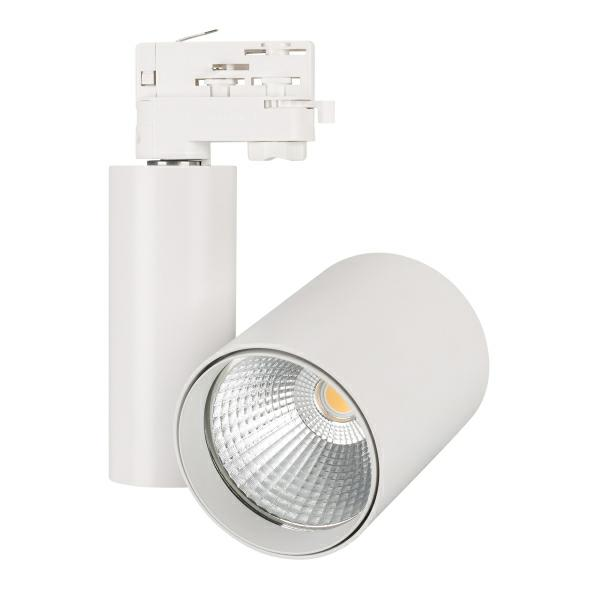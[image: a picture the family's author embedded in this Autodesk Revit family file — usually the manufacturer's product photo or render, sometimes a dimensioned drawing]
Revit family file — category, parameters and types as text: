
# Revit family: SHOP-4TR-R100
name_source: partatom
category: Осветительные приборы
revit_build: Autodesk Revit 2017 (Build: 20160225_1515(x64)
units: mm (PartAtom-declared; Revit-internal decimal feet)

## family parameters
Всегда вертикально = Да
Источник света = Нет
На основе рабочей плоскости = Нет
Общий = Нет
При загрузке вырезать с полостями = Нет
Размер круглого соединителя = Использовать диаметр
Тип детали = Нормальный
Точка расчета площади = Нет

## types (20) — shared parameters
ADSK_Единица измерения = шт.
ADSK_Завод-изготовитель = ARLIGHT
ADSK_Классификация нагрузок = Освещение
ADSK_Количество фаз = 1
ADSK_Количество фаз числовое = 1
ADSK_Коэффициент мощности = 0.95
ADSK_Наименование = Светильник
ADSK_Напряжение = 230 В
ADSK_Номинальная мощность = 40 Вт
ADSK_Полная мощность = 42 В·А
ADSK_Размер_Высота = 190 мм
ADSK_Размер_Диаметр = 100 мм
ADSK_Размер_Длина = 130 мм
ADSK_Размер_Радиус = 50 мм
ADSK_Размер_Ширина = 160 мм
ADSK_Ток = 0 А
ARL_Драйвер = Встроенный (30-42V, 1000mA)
ARL_Класс защиты от поражения электрическим током = I
ARL_Класс пылевлагозащиты = IP20
ARL_Область использования = Для локального освещения в торговых, демонстрационных, офисных, жилых и других помещениях
ARL_Рабочая температура окружающей среды = -25...+45 °C
ARL_Способ монтажа = на трек 3-фазный
ARL_Тип товара = Светильник
ARL_Угол обзора = 24°
URL = https://arlight.ru
Группа модели = Светильники
Изготовитель = ARLIGHT
Изготовитель (сайт) = www.arlight.ru
Изготовитель (телефон) = 8 800 505 26 29
Исходная интенсивность (лм) = 4000
Полная установленная мощность = 42 В·А
Разработчик = НТЦ Конструктор
Разработчик (URL) = https://constructor.ru
Разработчик (телефон) = +7 (495) 781-05-35

## per-type parameters (varying)
| type | ADSK_Код изделия | ADSK_Марка | ADSK_Масса_Текст | ARL_Индекс цветопередачи | ARL_Материал корпуса | ARL_Обозначение корпуса | ARL_Серия | ARL_Цвет покрытия | ARL_Цвет свечения | Комментарии к типоразмеру | Описание | Фотометрия | Цветовая температура (К) |
| 026278 Светильник LGD-SHOP-4TR-R100-40W White6000 (WH, 24 deg) | Арт. 026278 | LGD-SHOP-4TR-R100-40W White6000 | 1.32
1.332
1.332 | >90 | Металл, белый | Корпус круглый, металл, цвет белый | SHOP | Белый | Белый 6000K | Арт. 026278 | Светильник подвесной для треков/шин 4 провода, 40 Вт. Цвет свечения БЕЛЫЙ 6000K, световой поток 3600-4000лм, угол 24°, CRI>90. Корпус круглый, металл, цвет белый, IP20. Размеры ØDxHxL: Ø100х190х130 мм. Входное напряжение AC220-240V, мощность 40 Вт. Драйвер встроенный (30-42V, 1000mA) | SHOP-4TR-R100 IES Data : 026278_LGD-SHOP-4TR-R100-40W White6000 (WH, 24 deg) | 6000 |
| 025398 Светильник LGD-SHOP-4TR-R100-40W Day4000 (WH, 24 deg) | Арт. 025398 | LGD-SHOP-4TR-R100-40W Day4000 | 1.32
1.25
1.332 | >90 | Металл, белый | Корпус круглый, металл, цвет белый | SHOP | Белый | Дневной 4000K | Арт. 025398 | Светильник подвесной для треков/шин 4 провода, 40 Вт. Цвет свечения ДНЕВНОЙ 4000K, световой поток 3600-4000лм, угол 24°, CRI>90. Корпус круглый, металл, цвет белый, IP20. Размеры ØDxHxL: Ø100х190х130 мм. Входное напряжение AC220-240V, мощность 40 Вт. Драйвер встроенный (30-42V, 1000mA) | SHOP-4TR-R100 IES Data : 025398_LGD-SHOP-4TR-R100-40W Day4000 (WH, 24 deg) | 4000 |
| 026279 Светильник LGD-SHOP-4TR-R100-40W Warm3000 (WH, 24 deg) | Арт. 026279 | LGD-SHOP-4TR-R100-40W Warm3000 | 1.32
1.332
1.332 | >90 | Металл, белый | Корпус круглый, металл, цвет белый | SHOP | Белый | Теплый 3000K | Арт. 026279 | Светильник подвесной для треков/шин 4 провода, 40 Вт. Цвет свечения ТЕПЛЫЙ 3000K, световой поток 3600-4000лм, угол 24°, CRI>90. Корпус круглый, металл, цвет белый, IP20. Размеры ØDxHxL: Ø100х190х130 мм. Входное напряжение AC220-240V, мощность 40 Вт. Драйвер встроенный (30-42V, 1000mA) | SHOP-4TR-R100 IES Data : 026279_LGD-SHOP-4TR-R100-40W Warm3000 (WH, 24 deg) | 3000 |
| 026425 Светильник LGD-SHOP-PREMIUM-4TR-R100-40W Day4000 (WH, 24 deg) | Арт. 026425 | LGD-SHOP-PREMIUM-4TR-R100-40W Day4000 | 1.32
1.33
1.332 | >90 | Металл, белый | Корпус круглый, металл, цвет белый | SHOP | Белый | Дневной 4000K | Арт. 026425 | Светильник подвесной для треков/шин 4 провода, 40 Вт. Цвет свечения ДНЕВНОЙ 4000K, световой поток 3600-4000лм, угол 24°, CRI>90. Корпус круглый, металл, цвет белый, IP20. Размеры ØDxHxL: Ø100х190х130 мм. Входное напряжение AC220-240V, мощность 30 Вт. Драйвер встроенный (30-42V, 1000mA) | SHOP-4TR-R100 IES Data : 026425_LGD-SHOP-PREMIUM-4TR-R100-40W Day4000 (WH, 24 deg) | 4000 |
| 026426 Светильник LGD-SHOP-PREMIUM-4TR-R100-40W Warm3000 (WH, 24 deg) | Арт. 026426 | LGD-SHOP-PREMIUM-4TR-R100-40W Warm3000 | 1.32
1.332
1.332 | >90 | Металл, белый | Корпус круглый, металл, цвет белый | SHOP | Белый | Теплый 3000K | Арт. 026426 | Светильник подвесной для треков/шин 4 провода, 40 Вт. Цвет свечения ТЕПЛЫЙ 3000K, световой поток 3600-4000лм, угол 24°, CRI>90. Корпус круглый, металл, цвет белый, IP20. Размеры ØDxHxL: Ø100х190х130 мм. Входное напряжение AC220-240V, мощность 40 Вт. Драйвер встроенный (30-42V, 1000mA) | SHOP-4TR-R100 IES Data : 026426_LGD-SHOP-PREMIUM-4TR-R100-40W Warm3000 (WH, 24 deg) | 3000 |
| 026281 Светильник LGD-SHOP-4TR-R100-40W White6000 (BK, 24 deg) | Арт. 026281 | LGD-SHOP-4TR-R100-40W White6000 | 1.32
1.332
1.332 | >90 | Металл, чёрный | Корпус круглый, металл, цвет черный | SHOP | Черный | Белый 6000K | Арт. 026281 | Светильник подвесной для треков/шин 4 провода, 40 Вт. Цвет свечения БЕЛЫЙ 6000K, световой поток 3600-4000лм, угол 24°, CRI>90. Корпус круглый, металл, цвет черный, IP20. Размеры ØDxHxL: Ø100х190х130 мм. Входное напряжение AC220-240V, мощность 40 Вт. Драйвер встроенный (30-42V, 1000mA) | SHOP-4TR-R100 IES Data : 026281_LGD-SHOP-4TR-R100-40W White6000 (BK, 24 deg) | 6000 |
| 026282 Светильник LGD-SHOP-4TR-R100-40W Day4000 (BK, 24 deg) | Арт. 026282 | LGD-SHOP-4TR-R100-40W Day4000 | 1.32
1.332
1.332 | >90 | Металл, чёрный | Корпус круглый, металл, цвет черный | SHOP | Черный | Дневной 4000K | Арт. 026282 | Светильник подвесной для треков/шин 4 провода, 40 Вт. Цвет свечения ДНЕВНОЙ 4000K, световой поток 3600-4000лм, угол 24°, CRI>90. Корпус круглый, металл, цвет черный, IP20. Размеры ØDxHxL: Ø100х190х130 мм. Входное напряжение AC220-240V, мощность 40 Вт. Драйвер встроенный (30-42V, 1000mA) | SHOP-4TR-R100 IES Data : 026282_LGD-SHOP-4TR-R100-40W Day4000 (BK, 24 deg) | 4000 |
| 026284 Светильник LGD-SHOP-4TR-R100-40W Warm3000 (BK, 24 deg) | Арт. 026284 | LGD-SHOP-4TR-R100-40W Warm3000 | 1.32
1.332
1.332 | >90 | Металл, чёрный | Корпус круглый, металл, цвет черный | SHOP | Черный | Теплый 3000K | Арт. 026284 | Светильник подвесной для треков/шин 4 провода, 40 Вт. Цвет свечения ТЕПЛЫЙ 3000K, световой поток 3600-4000лм, угол 24°, CRI>90. Корпус круглый, металл, цвет черный, IP20. Размеры ØDxHxL: Ø100х190х130 мм. Входное напряжение AC220-240V, мощность 40 Вт. Драйвер встроенный (30-42V, 1000mA) | SHOP-4TR-R100 IES Data : 026284_LGD-SHOP-4TR-R100-40W Warm3000 (BK, 24 deg) | 3000 |
| 026428 Светильник LGD-SHOP-PREMIUM-4TR-R100-40W Day4000 (BK, 24 deg) | Арт. 026428 | LGD-SHOP-PREMIUM-4TR-R100-40W Day4000 | 1.32
1.332
1.332 | >90 | Металл, чёрный | Корпус круглый, металл, цвет черный | SHOP | Черный | Дневной 4000K | Арт. 026428 | Светильник подвесной для треков/шин 4 провода, 40 Вт. Цвет свечения ДНЕВНОЙ 4000K, световой поток 3600-4000лм, угол 24°, CRI>90. Корпус круглый, металл, цвет черный, IP20. Размеры ØDxHxL: Ø100х190х130 мм. Входное напряжение AC220-240V, мощность 40 Вт. Драйвер встроенный (30-42V, 1000mA) | SHOP-4TR-R100 IES Data : 026428_LGD-SHOP-PREMIUM-4TR-R100-40W Day4000 (BK, 24 deg) | 4000 |
| 026429 Светильник LGD-SHOP-PREMIUM-4TR-R100-40W Warm3000 (BK, 24 deg) | Арт. 026429 | LGD-SHOP-PREMIUM-4TR-R100-40W Warm3000 | 1.32
1.332
1.332 | >90 | Металл, чёрный | Корпус круглый, металл, цвет черный | SHOP | Черный | Теплый 3000K | Арт. 026429 | Светильник подвесной для треков/шин 4 провода, 40 Вт. Цвет свечения ТЕПЛЫЙ 3000K, световой поток 3600-4000лм, угол 24°, CRI>90. Корпус круглый, металл, цвет черный, IP20. Размеры ØDxHxL: Ø100х190х130 мм. Входное напряжение AC220-240V, мощность 40 Вт. Драйвер встроенный (30-42V, 1000mA) | SHOP-4TR-R100 IES Data : 026429_LGD-SHOP-PREMIUM-4TR-R100-40W Warm3000 (BK, 24 deg) | 3000 |
| 026387 Светильник LGD-SHOP-4TR-R100-40W Cool SP7500-Fish (WH, 24 deg) | Арт. 026387 | LGD-SHOP-4TR-R100-40W Cool SP7500-Fish | 1.32
1.35
1.332 | >90 | Металл, белый | Корпус круглый, металл, цвет белый | SHOP FOOD | Белый | Холодный 8000K | Арт. 026387 | Светильник подвесной для треков/шин 4 провода, 40 Вт. Цвет свечения СПЕЦИАЛЬНЫЙ ХОЛОДНЫЙ 7500K для рыбы и морепродуктов, световой поток 3600-4000лм, угол 24°, CRI>90. Корпус круглый, металл, цвет белый, IP20. Размеры DxHxL: 100х190х130 мм. Входное напряжение AC220-240V, мощность 40 Вт. Драйвер встроенный (30-42V, 1000mA) | SHOP-4TR-R100 IES Data : 026387_LGD-SHOP-4TR-R100-40W Cool SP7500-Fish (WH, 24 deg) | 8000 |
| 026423 Светильник LGD-SHOP-4TR-R100-40W Day SP5000-Veg (WH, 24 deg) | Арт. 026423 | LGD-SHOP-4TR-R100-40W Day SP5000-Veg | 1.32
1.35
1.332 | >90 | Металл, белый | Корпус круглый, металл, цвет белый | SHOP FOOD | Белый | Дневной 5000K | Арт. 026423 | Светильник подвесной для треков/шин 4 провода, 40 Вт. Цвет свечения СПЕЦИАЛЬНЫЙ ДНЕВНОЙ 5000K для зеленых овощей и фруктов, световой поток 3600-4000лм, угол 24°, CRI>90. Корпус круглый, металл, цвет белый, IP20. Размеры DxHxL: 100х190х130 мм. Входное напряжение AC220-240V, мощность 40 Вт. Драйвер встроенный (30-42V, 1000mA) | SHOP-4TR-R100 IES Data : 026423_LGD-SHOP-4TR-R100-40W Day SP5000-Veg (WH, 24 deg) | 5000 |
| 026289 Светильник LGD-SHOP-4TR-R100-40W Warm SP3000-Fruit (WH, 24 deg) | Арт. 026289 | LGD-SHOP-4TR-R100-40W Warm SP3000-Fruit | 1.32
1.35
1.332 | >90 | Металл, белый | Корпус круглый, металл, цвет белый | SHOP FOOD | Белый | Теплый 3000K | Арт. 026289 | Светильник подвесной для треков/шин 4 провода, 40 Вт. Цвет свечения СПЕЦИАЛЬНЫЙ ТЕПЛЫЙ 3000K для красных и желтых фруктов и овощей, световой поток 3600-4000лм, угол 24°, CRI>90. Корпус круглый, металл, цвет белый, IP20. Размеры DxHxL: 100х190х130 мм. Входное напряжение AC220-240V, мощность 40 Вт. Драйвер встроенный (30-42V, 1000mA) | SHOP-4TR-R100 IES Data : 026289_LGD-SHOP-4TR-R100-40W Warm SP3000-Fruit (WH, 24 deg) | 3000 |
| 026288 Светильник LGD-SHOP-4TR-R100-40W Warm SP2900-Meat (WH, 24 deg) | Арт. 026288 | LGD-SHOP-4TR-R100-40W Warm SP2900-Meat | 1.32
1.35
1.332 | >65 | Металл, белый | Корпус круглый, металл, цвет белый | SHOP FOOD | Белый | Теплый 2700K | Арт. 026288 | Светильник подвесной для треков/шин 4 провода, 40 Вт. Цвет свечения СПЕЦИАЛЬНЫЙ ТЕПЛЫЙ с розовым оттенком 2900K для мяса, световой поток 3600-4000лм, угол 24°, CRI>65. Корпус круглый, металл, цвет белый, IP20. Размеры DxHxL: 100х190х130 мм. Входное напряжение AC220-240V, мощность 40 Вт. Драйвер встроенный (30-42V, 1000mA) | SHOP-4TR-R100 IES Data : 026288_LGD-SHOP-4TR-R100-40W Warm SP2900-Meat (WH, 24 deg) | 2700 |
| 026388 Светильник LGD-SHOP-4TR-R100-40W Warm SP2500-Bread (WH, 24 deg) | Арт. 026388 | LGD-SHOP-4TR-R100-40W Warm SP2500-Bread | 1.32
1.35
1.35 | 95..98 | Металл, белый | Корпус круглый, металл, цвет белый | SHOP FOOD | Белый | Теплый 2400K | Арт. 026388 | Светильник подвесной для треков/шин 4 провода, 40 Вт. Цвет свечения СПЕЦИАЛЬНЫЙ ТЕПЛЫЙ 2500K для выпечки, световой поток 3600-4000лм, угол 24°, CRI>96. Корпус круглый, металл, цвет белый, IP20. Размеры DxHxL: 100х190х130 мм. Входное напряжение AC220-240V, мощность 40 Вт. Драйвер встроенный (30-42V, 1000mA) | SHOP-4TR-R100 IES Data : 026388_LGD-SHOP-4TR-R100-40W Warm SP2500-Bread (WH, 24 deg) | 2400 |
| 026291 Светильник LGD-SHOP-4TR-R100-40W Cool SP7500-Fish (BK, 24 deg) | Арт. 026291 | LGD-SHOP-4TR-R100-40W Cool SP7500-Fish | 1.32
1.332
1.332 | >90 | Металл, чёрный | Корпус круглый, металл, цвет черный | SHOP FOOD | Черный | Холодный 8000K | Арт. 026291 | Светильник подвесной для треков/шин 4 провода, 40 Вт. Цвет свечения СПЕЦИАЛЬНЫЙ ХОЛОДНЫЙ 7500K для рыбы и морепродуктов, световой поток 3600-4000лм, угол 24°, CRI>90. Корпус круглый, металл, цвет черный, IP20. Размеры DxHxL: 100х190х130 мм. Входное напряжение AC220-240V, мощность 40 Вт. Драйвер встроенный (30-42V, 1000mA) | SHOP-4TR-R100 IES Data : 026291_LGD-SHOP-4TR-R100-40W Cool SP7500-Fish (BK, 24 deg) | 8000 |
| 026422 Светильник LGD-SHOP-4TR-R100-40W Day SP5000-Veg (BK, 24 deg) | Арт. 026422 | LGD-SHOP-4TR-R100-40W Day SP5000-Veg | 1.32
1.332
1.332 | >90 | Металл, чёрный | Корпус круглый, металл, цвет черный | SHOP FOOD | Черный | Дневной 5000K | Арт. 026422 | Светильник подвесной для треков/шин 4 провода, 40 Вт. Цвет свечения СПЕЦИАЛЬНЫЙ ДНЕВНОЙ 5000K для зеленых овощей и фруктов, световой поток 3600-4000лм, угол 24°, CRI>90. Корпус круглый, металл, цвет черный, IP20. Размеры DxHxL: 100х190х130 мм. Входное напряжение AC220-240V, мощность 40 Вт. Драйвер встроенный (30-42V, 1000mA) | SHOP-4TR-R100 IES Data : 026422_LGD-SHOP-4TR-R100-40W Day SP5000-Veg (BK, 24 deg) | 5000 |
| 026292 Светильник LGD-SHOP-4TR-R100-40W Warm SP3000-Fruit (BK, 24 deg) | Арт. 026292 | LGD-SHOP-4TR-R100-40W Warm SP3000-Fruit | 1.32
1.332
1.332 | >90 | Металл, чёрный | Корпус круглый, металл, цвет черный | SHOP FOOD | Черный | Теплый 3000K | Арт. 026292 | Светильник подвесной для треков/шин 4 провода, 40 Вт. Цвет свечения СПЕЦИАЛЬНЫЙ ТЕПЛЫЙ 3000K для красных и желтых фруктов и овощей, световой поток 3600-4000лм, угол 24°, CRI>90. Корпус круглый, металл, цвет черный, IP20. Размеры DxHxL: 100х190х130 мм. Входное напряжение AC220-240V, мощность 40 Вт. Драйвер встроенный (30-42V, 1000mA) | SHOP-4TR-R100 IES Data : 026292_LGD-SHOP-4TR-R100-40W Warm SP3000-Fruit (BK, 24 deg) | 3000 |
| 026290 Светильник LGD-SHOP-4TR-R100-40W Warm SP2900-Meat (BK, 24 deg) | Арт. 026290 | LGD-SHOP-4TR-R100-40W Warm SP2900-Meat | 1.32
1.332
1.332 | >65 | Металл, чёрный | Корпус круглый, металл, цвет черный | SHOP FOOD | Черный | Теплый 2700K | Арт. 026290 | Светильник подвесной для треков/шин 4 провода, 40 Вт. Цвет свечения СПЕЦИАЛЬНЫЙ ТЕПЛЫЙ с розовым оттенком 2900K для мяса, световой поток 3600-4000лм, угол 24°, CRI>65. Корпус круглый, металл, цвет черный, IP20. Размеры DxHxL: 100х190х130 мм. Входное напряжение AC220-240V, мощность 40 Вт. Драйвер встроенный (30-42V, 1000mA) | SHOP-4TR-R100 IES Data : 026290_LGD-SHOP-4TR-R100-40W Warm SP2900-Meat (BK, 24 deg) | 2700 |
| 026386 Светильник LGD-SHOP-4TR-R100-40W Warm SP2500-Bread (BK, 24 deg) | Арт. 026386 | LGD-SHOP-4TR-R100-40W Warm SP2500-Bread | 1.32
1.332
1.332 | 95..98 | Металл, чёрный | Корпус круглый, металл, цвет черный | SHOP FOOD | Черный | Теплый 2400K | Арт. 026386 | Светильник подвесной для треков/шин 4 провода, 40 Вт. Цвет свечения СПЕЦИАЛЬНЫЙ ТЕПЛЫЙ 2500K для выпечки, световой поток 3600-4000лм, угол 24°, CRI>96. Корпус круглый, металл, цвет черный, IP20. Размеры DxHxL: 100х190х130 мм. Входное напряжение AC220-240V, мощность 40 Вт. Драйвер встроенный (30-42V, 1000mA) | SHOP-4TR-R100 IES Data : 026386_LGD-SHOP-4TR-R100-40W Warm SP2500-Bread (BK, 24 deg) | 2400 |

## geometry (parser evidence)
native form markers: Sweep x1
no freeform markers — native parametric forms only
